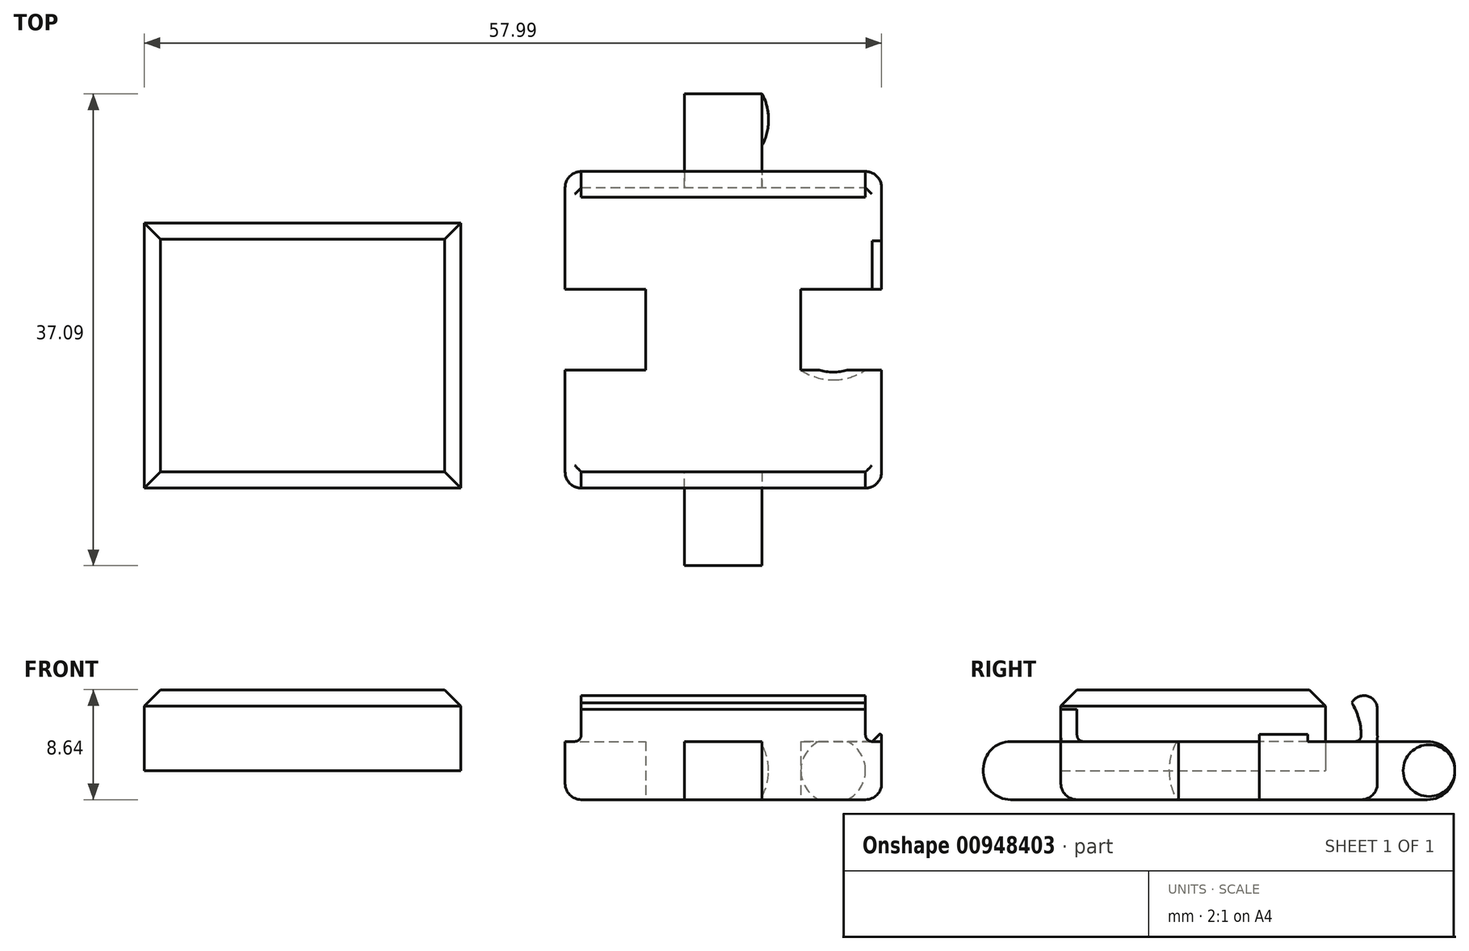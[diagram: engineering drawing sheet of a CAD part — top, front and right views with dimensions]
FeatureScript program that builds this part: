
annotation { "Feature Type Name" : "Feature", "Feature Type Description" : "" }
export const myFeature = defineFeature(function(context is Context, id is Id, definition is map)
    precondition{}
    {
        {
            var Q0;
            Q0=qCreatedBy(makeId("Top.planeOp"),FACE);
            var sketch = newSketch(context, id + "F0", { "sketchPlane" : qUnion([Q0])});
            skLineSegment(sketch, "E0.bottom", {"start": v(0, 0) * mm, "end": v(9.4, 0) * mm});
            skLineSegment(sketch, "E0.top", {"start": v(0, 24.9) * mm, "end": v(9.4, 24.9) * mm});
            skLineSegment(sketch, "E0.left", {"start": v(0, 0) * mm, "end": v(0, 9.27) * mm});
            skLineSegment(sketch, "E1", {"start": v(0, 12.45) * mm, "end": v(24.9, 12.45) * mm, "construction": true});
            skLineSegment(sketch, "E2", {"start": v(12.45, 24.9) * mm, "end": v(12.45, 0) * mm, "construction": true});
            skLineSegment(sketch, "E3", {"start": v(9.4, 24.9) * mm, "end": v(9.4, 30.99) * mm});
            skLineSegment(sketch, "E4", {"start": v(9.4, 30.99) * mm, "end": v(15.5, 30.99) * mm});
            skLineSegment(sketch, "E5", {"start": v(15.5, 30.99) * mm, "end": v(15.5, 24.9) * mm});
            skLineSegment(sketch, "E6", {"start": v(9.4, 0) * mm, "end": v(9.4, -6.1) * mm});
            skLineSegment(sketch, "E7", {"start": v(9.4, -6.1) * mm, "end": v(15.5, -6.1) * mm});
            skLineSegment(sketch, "E8", {"start": v(15.5, -6.1) * mm, "end": v(15.5, 0) * mm});
            skLineSegment(sketch, "E9.trimOffspring", {"start": v(15.5, 24.9) * mm, "end": v(24.9, 24.9) * mm});
            skLineSegment(sketch, "E10.trimOffspring", {"start": v(15.5, 0) * mm, "end": v(24.9, 0) * mm});
            skLineSegment(sketch, "E11", {"start": v(24.9, 15.62) * mm, "end": v(18.54, 15.62) * mm});
            skLineSegment(sketch, "E12", {"start": v(18.54, 15.62) * mm, "end": v(18.54, 9.27) * mm});
            skLineSegment(sketch, "E13", {"start": v(18.54, 9.27) * mm, "end": v(24.9, 9.27) * mm});
            skLineSegment(sketch, "E14", {"start": v(0, 15.62) * mm, "end": v(6.35, 15.62) * mm});
            skLineSegment(sketch, "E15", {"start": v(6.35, 15.62) * mm, "end": v(6.35, 9.27) * mm});
            skLineSegment(sketch, "E16", {"start": v(6.35, 9.27) * mm, "end": v(0, 9.27) * mm});
            skLineSegment(sketch, "E17.trimOffspring", {"start": v(0, 15.62) * mm, "end": v(0, 24.9) * mm});
            skLineSegment(sketch, "E18.trimOffspring", {"start": v(24.9, 15.62) * mm, "end": v(24.9, 24.9) * mm});
            skLineSegment(sketch, "E19", {"start": v(24.9, 0) * mm, "end": v(24.9, 9.27) * mm});
            skLineSegment(sketch, "E20", {"start": v(24.9, 9.27) * mm, "end": v(24.9, 15.62) * mm, "construction": true});
            skLineSegment(sketch, "E21", {"start": v(0, 9.27) * mm, "end": v(0, 15.62) * mm, "construction": true});
            skSolve(sketch);
        }
        {
            var Q0;
            Q0=makeQuery(id+"F0.imprint","IMPRINT",FACE,{"disambiguationData":[TD([[makeQuery(id+"F0.imprint","IMPRINT",EDGE,{"derivedFrom":sQuery(id+"F0.wireOp",EDGE,"E0.bottom")}),1.0]])]});
            extrude(context, id + "F1", {"entities" : qUnion([Q0]), "depth" : 4.57 * mm, "offsetDistance" : 25.4 * mm});
        }
        {
            var Q0;
            Q0=makeQuery(id+"F1.opExtrude","CAP_EDGE",EDGE,{"disambiguationData":[OSD([sQuery(id+"F0.wireOp",EDGE,"E4")])],"isStart":false});
            var Q1;
            Q1=makeQuery(id+"F1.opExtrude","CAP_EDGE",EDGE,{"disambiguationData":[OSD([sQuery(id+"F0.wireOp",EDGE,"E7")])],"isStart":false});
            var Q2;
            Q2=makeQuery(id+"F1.opExtrude","CAP_EDGE",EDGE,{"disambiguationData":[OSD([sQuery(id+"F0.wireOp",EDGE,"E7")])],"isStart":true});
            var Q3;
            Q3=makeQuery(id+"F1.opExtrude","CAP_EDGE",EDGE,{"disambiguationData":[OSD([sQuery(id+"F0.wireOp",EDGE,"E4")])],"isStart":true});
            fillet(context, id + "F2", {"entities" : qUnion([Q0, Q1, Q2, Q3]), "radius" : 2.16 * mm, "tangentPropagation" : true, "allowEdgeOverflow" : false});
        }
        {
            var Q0;
            Q0=makeQuery(id+"F1.opExtrude","CAP_EDGE",EDGE,{"disambiguationData":[OSD([sQuery(id+"F0.wireOp",EDGE,"E0.top")])],"isStart":true});
            var Q1;
            Q1=makeQuery(id+"F1.opExtrude","CAP_EDGE",EDGE,{"disambiguationData":[OSD([sQuery(id+"F0.wireOp",EDGE,"E9.trimOffspring")])],"isStart":true});
            var Q2;
            Q2=makeQuery(id+"F1.opExtrude","CAP_EDGE",EDGE,{"disambiguationData":[OSD([sQuery(id+"F0.wireOp",EDGE,"E10.trimOffspring")])],"isStart":true});
            var Q3;
            Q3=makeQuery(id+"F1.opExtrude","CAP_EDGE",EDGE,{"disambiguationData":[OSD([sQuery(id+"F0.wireOp",EDGE,"E0.bottom")])],"isStart":true});
            fillet(context, id + "F3", {"entities" : qUnion([Q0, Q1, Q2, Q3]), "radius" : 1.27 * mm, "tangentPropagation" : true, "allowEdgeOverflow" : false});
        }
        {
            var Q0;
            Q0=makeQuery(id+"F1.opExtrude","CAP_FACE",FACE,{"disambiguationData":[OSD([sQuery(id+"F0.wireOp",EDGE,"E0.bottom"),sQuery(id+"F0.wireOp",EDGE,"E0.top"),sQuery(id+"F0.wireOp",EDGE,"E0.left"),sQuery(id+"F0.wireOp",EDGE,"E3"),sQuery(id+"F0.wireOp",EDGE,"E4"),sQuery(id+"F0.wireOp",EDGE,"E5"),sQuery(id+"F0.wireOp",EDGE,"E6"),sQuery(id+"F0.wireOp",EDGE,"E7"),sQuery(id+"F0.wireOp",EDGE,"E8"),sQuery(id+"F0.wireOp",EDGE,"E9.trimOffspring"),sQuery(id+"F0.wireOp",EDGE,"E10.trimOffspring"),sQuery(id+"F0.wireOp",EDGE,"E11"),sQuery(id+"F0.wireOp",EDGE,"E12"),sQuery(id+"F0.wireOp",EDGE,"E13"),sQuery(id+"F0.wireOp",EDGE,"E14"),sQuery(id+"F0.wireOp",EDGE,"E15"),sQuery(id+"F0.wireOp",EDGE,"E16"),sQuery(id+"F0.wireOp",EDGE,"E17.trimOffspring"),sQuery(id+"F0.wireOp",EDGE,"E18.trimOffspring"),sQuery(id+"F0.wireOp",EDGE,"E19")])],"isStart":true});
            cPlane(context, id + "F4", {"entities" : qUnion([Q0]), "cplaneType" : CPlaneType.OFFSET, "offset" : 2.3 * mm, "oppositeDirection" : true, "width" : 152.4 * mm, "height" : 152.4 * mm});
        }
        {
            var Q0;
            Q0=qCreatedBy(id+"F4.planeOp",FACE);
            var sketch = newSketch(context, id + "F5", { "sketchPlane" : qUnion([Q0])});
            skLineSegment(sketch, "E22", {"start": v(9.9, -28.96) * mm, "end": v(17.45, -28.96) * mm, "construction": true});
            skLineSegment(sketch, "E23.0", {"start": v(9.4, -28.83) * mm, "end": v(9.4, -28.83) * mm});
            skLineSegment(sketch, "E24", {"start": v(15.5, -30.99) * mm, "end": v(9.14, -30.99) * mm, "construction": true});
            skLineSegment(sketch, "E25.0", {"start": v(15.5, -28.83) * mm, "end": v(15.5, -30.99) * mm, "construction": true});
            skLineSegment(sketch, "E26", {"start": v(15.5, -28.96) * mm, "end": v(16, -28.96) * mm});
            skArc(sketch, "E27", {"start": v(15.5, -30.99) * mm, "mid": v(15.87, -30) * mm, "end": v(16, -28.96) * mm});
            skLineSegment(sketch, "E28", {"start": v(15.5, -30.99) * mm, "end": v(15.5, -28.96) * mm});
            skSolve(sketch);
        }
        {
            var Q0;
            Q0=makeQuery(id+"F5.imprint","IMPRINT",FACE,{"disambiguationData":[TD([[makeQuery(id+"F5.imprint","IMPRINT",EDGE,{"derivedFrom":sQuery(id+"F5.wireOp",EDGE,"E26")}),-1.0]])]});
            var Q1;
            Q1=sQuery(id+"F5.wireOp",EDGE,"E27");
            var Q2;
            Q2=sQuery(id+"F5.wireOp",EDGE,"E22");
            revolve(context, id + "F6", {"operationType" : NewBodyOperationType.ADD, "surfaceOperationType" : NewSurfaceOperationType.NEW, "entities" : qUnion([Q0]), "surfaceEntities" : qUnion([Q1]), "axis" : qUnion([Q2]), "revolveType" : RevolveType.FULL});
        }
        {
            var Q0;
            Q0=makeQuery(id+"F1.opExtrude","SWEPT_FACE",FACE,{"disambiguationData":[OSD([sQuery(id+"F0.wireOp",EDGE,"E9.trimOffspring")])]});
            cPlane(context, id + "F7", {"entities" : qUnion([Q0]), "cplaneType" : CPlaneType.OFFSET, "offset" : 12.45 * mm, "oppositeDirection" : true, "width" : 152.4 * mm, "height" : 152.4 * mm});
        }
        {
            var Q0;
            Q0=makeQuery(id+"F1.opExtrude","CAP_EDGE",EDGE,{"disambiguationData":[OSD([sQuery(id+"F0.wireOp",EDGE,"E19")])],"isStart":true});
            var Q1;
            Q1=makeQuery(id+"F1.opExtrude","CAP_EDGE",EDGE,{"disambiguationData":[OSD([sQuery(id+"F0.wireOp",EDGE,"E18.trimOffspring")])],"isStart":true});
            var Q2;
            Q2=makeQuery(id+"F1.opExtrude","CAP_EDGE",EDGE,{"disambiguationData":[OSD([sQuery(id+"F0.wireOp",EDGE,"E17.trimOffspring")])],"isStart":true});
            var Q3;
            Q3=makeQuery(id+"F1.opExtrude","CAP_EDGE",EDGE,{"disambiguationData":[OSD([sQuery(id+"F0.wireOp",EDGE,"E0.left")])],"isStart":true});
            fillet(context, id + "F8", {"entities" : qUnion([Q0, Q1, Q2, Q3]), "radius" : 1.27 * mm, "tangentPropagation" : true, "allowEdgeOverflow" : false});
        }
        {
            var Q0;
            Q0=qCreatedBy(id+"F4.planeOp",FACE);
            var sketch = newSketch(context, id + "F9", { "sketchPlane" : qUnion([Q0])});
            skPoint(sketch, "E29.0", {"position": v(18.54, -12.45) * mm});
            skLineSegment(sketch, "E30.0", {"start": v(18.54, -15.62) * mm, "end": v(18.54, -9.27) * mm, "construction": true});
            skLineSegment(sketch, "E31.0", {"start": v(18.54, -9.27) * mm, "end": v(23.62, -9.27) * mm, "construction": true});
            skLineSegment(sketch, "E32.0", {"start": v(23.62, -15.62) * mm, "end": v(18.54, -15.62) * mm, "construction": true});
            skLineSegment(sketch, "E33", {"start": v(18.54, -9.27) * mm, "end": v(21.08, -9.27) * mm});
            skLineSegment(sketch, "E34", {"start": v(21.08, -9.27) * mm, "end": v(21.08, -8.5) * mm});
            skArc(sketch, "E35", {"start": v(21.08, -8.5) * mm, "mid": v(19.76, -8.7) * mm, "end": v(18.54, -9.27) * mm});
            skLineSegment(sketch, "E36", {"start": v(21.08, -9.27) * mm, "end": v(21.08, -12.64) * mm, "construction": true});
            skSolve(sketch);
        }
        {
            var Q0;
            Q0=makeQuery(id+"F9.imprint","IMPRINT",FACE,{"disambiguationData":[TD([[makeQuery(id+"F9.imprint","IMPRINT",EDGE,{"derivedFrom":sQuery(id+"F9.wireOp",EDGE,"E33")}),1.0]])]});
            var Q1;
            Q1=sQuery(id+"F9.wireOp",EDGE,"E36");
            revolve(context, id + "F10", {"operationType" : NewBodyOperationType.REMOVE, "surfaceOperationType" : NewSurfaceOperationType.NEW, "entities" : qUnion([Q0]), "axis" : qUnion([Q1]), "revolveType" : RevolveType.FULL, "oppositeDirection" : true});
        }
        {
            var Q0;
            Q0=makeQuery(id+"F1.opExtrude","SWEPT_FACE",FACE,{"disambiguationData":[OSD([sQuery(id+"F0.wireOp",EDGE,"E18.trimOffspring")])]});
            cPlane(context, id + "F11", {"entities" : qUnion([Q0]), "cplaneType" : CPlaneType.OFFSET, "offset" : 12.45 * mm, "oppositeDirection" : true, "width" : 152.4 * mm, "height" : 152.4 * mm});
        }
        {
            var Q0;
            Q0=makeQuery(id+"F1.opExtrude","CAP_FACE",FACE,{"disambiguationData":[OSD([sQuery(id+"F0.wireOp",EDGE,"E0.bottom"),sQuery(id+"F0.wireOp",EDGE,"E0.top"),sQuery(id+"F0.wireOp",EDGE,"E0.left"),sQuery(id+"F0.wireOp",EDGE,"E3"),sQuery(id+"F0.wireOp",EDGE,"E4"),sQuery(id+"F0.wireOp",EDGE,"E5"),sQuery(id+"F0.wireOp",EDGE,"E6"),sQuery(id+"F0.wireOp",EDGE,"E7"),sQuery(id+"F0.wireOp",EDGE,"E8"),sQuery(id+"F0.wireOp",EDGE,"E9.trimOffspring"),sQuery(id+"F0.wireOp",EDGE,"E10.trimOffspring"),sQuery(id+"F0.wireOp",EDGE,"E11"),sQuery(id+"F0.wireOp",EDGE,"E12"),sQuery(id+"F0.wireOp",EDGE,"E13"),sQuery(id+"F0.wireOp",EDGE,"E14"),sQuery(id+"F0.wireOp",EDGE,"E15"),sQuery(id+"F0.wireOp",EDGE,"E16"),sQuery(id+"F0.wireOp",EDGE,"E17.trimOffspring"),sQuery(id+"F0.wireOp",EDGE,"E18.trimOffspring"),sQuery(id+"F0.wireOp",EDGE,"E19")])],"isStart":false});
            var sketch = newSketch(context, id + "F12", { "sketchPlane" : qUnion([Q0])});
            skLineSegment(sketch, "E37.bottom", {"start": v(1.27, 0) * mm, "end": v(23.62, 0) * mm});
            skLineSegment(sketch, "E37.top", {"start": v(1.27, 1.27) * mm, "end": v(23.62, 1.27) * mm});
            skLineSegment(sketch, "E37.left", {"start": v(1.27, 0) * mm, "end": v(1.27, 1.27) * mm});
            skLineSegment(sketch, "E37.right", {"start": v(23.62, 0) * mm, "end": v(23.62, 1.27) * mm});
            skLineSegment(sketch, "E38.bottom", {"start": v(1.27, 24.9) * mm, "end": v(23.62, 24.9) * mm});
            skLineSegment(sketch, "E38.top", {"start": v(1.27, 23.62) * mm, "end": v(23.62, 23.62) * mm});
            skLineSegment(sketch, "E38.left", {"start": v(1.27, 24.9) * mm, "end": v(1.27, 23.62) * mm});
            skLineSegment(sketch, "E38.right", {"start": v(23.62, 24.9) * mm, "end": v(23.62, 23.62) * mm});
            skLineSegment(sketch, "E39", {"start": v(12.45, 28.83) * mm, "end": v(12.45, -3.94) * mm, "construction": true});
            skLineSegment(sketch, "E40", {"start": v(18.54, 12.45) * mm, "end": v(6.35, 12.45) * mm, "construction": true});
            skLineSegment(sketch, "E41", {"start": v(1.27, 1.27) * mm, "end": v(1.27, 23.62) * mm, "construction": true});
            skLineSegment(sketch, "E42", {"start": v(23.62, 1.27) * mm, "end": v(23.62, 23.62) * mm, "construction": true});
            skSolve(sketch);
        }
        {
            var Q0;
            Q0=makeQuery(id+"F12.imprint","IMPRINT",FACE,{"disambiguationData":[TD([[makeQuery(id+"F12.imprint","IMPRINT",EDGE,{"derivedFrom":sQuery(id+"F12.wireOp",EDGE,"E37.top")}),-1.0]])]});
            var Q1;
            Q1=makeQuery(id+"F12.imprint","IMPRINT",FACE,{"disambiguationData":[TD([[makeQuery(id+"F12.imprint","IMPRINT",EDGE,{"derivedFrom":sQuery(id+"F12.wireOp",EDGE,"E38.top")}),1.0]])]});
            extrude(context, id + "F13", {"entities" : qUnion([Q0, Q1]), "operationType" : NewBodyOperationType.ADD, "depth" : 2.54 * mm, "offsetDistance" : 25.4 * mm});
        }
        {
            var Q0;
            Q0=makeQuery(id+"F13.opExtrude","SWEPT_FACE",FACE,{"disambiguationData":[OSD([sQuery(id+"F12.wireOp",EDGE,"E37.right")])]});
            var sketch = newSketch(context, id + "F14", { "sketchPlane" : qUnion([Q0])});
            skLineSegment(sketch, "E43", {"start": v(0, 7.11) * mm, "end": v(1.07, 7.11) * mm, "construction": true});
            skArc(sketch, "E44", {"start": v(0, 7.11) * mm, "mid": v(0.8, 8.15) * mm, "end": v(2, 7.61) * mm});
            skLineSegment(sketch, "E45", {"start": v(1.07, 7.11) * mm, "end": v(2, 7.61) * mm, "construction": true});
            skLineSegment(sketch, "E46", {"start": v(1.27, 7.11) * mm, "end": v(2, 7.61) * mm});
            skLineSegment(sketch, "E47.1", {"start": v(24.9, 7.11) * mm, "end": v(24.9, 4.57) * mm, "construction": true});
            skArc(sketch, "E48", {"start": v(24.9, 7.11) * mm, "mid": v(24.08, 8.15) * mm, "end": v(22.88, 7.61) * mm, "construction": true});
            skLineSegment(sketch, "E49", {"start": v(23.83, 7.11) * mm, "end": v(22.88, 7.61) * mm, "construction": true});
            skArc(sketch, "E50", {"start": v(24.9, 7.11) * mm, "mid": v(24.08, 8.15) * mm, "end": v(22.88, 7.61) * mm});
            skLineSegment(sketch, "E51", {"start": v(23.62, 7.11) * mm, "end": v(22.88, 7.61) * mm});
            skLineSegment(sketch, "E52", {"start": v(23.62, 7.11) * mm, "end": v(24.9, 7.11) * mm});
            skSolve(sketch);
        }
        {
            var Q0;
            Q0=makeQuery(id+"F14.imprint","IMPRINT",FACE,{"disambiguationData":[TD([[makeQuery(id+"F14.imprint","IMPRINT",EDGE,{"derivedFrom":sQuery(id+"F14.wireOp",EDGE,"E44")}),-1.0]])]});
            var Q1;
            Q1=makeQuery(id+"F14.imprint","IMPRINT",FACE,{"disambiguationData":[TD([[makeQuery(id+"F14.imprint","IMPRINT",EDGE,{"derivedFrom":sQuery(id+"F14.wireOp",EDGE,"E50")}),1.0]])]});
            extrude(context, id + "F15", {"entities" : qUnion([Q0, Q1]), "operationType" : NewBodyOperationType.ADD, "oppositeDirection" : true, "depth" : 22.35 * mm, "offsetDistance" : 25.4 * mm});
        }
        {
            var Q0;
            Q0=makeQuery(id+"F15.boolean.opBoolean","MERGE",EDGE,{"derivedFrom":[makeQuery(id+"F13.opExtrude","CAP_EDGE",EDGE,{"disambiguationData":[OSD([sQuery(id+"F12.wireOp",EDGE,"E38.top")])],"isStart":false}),makeQuery(id+"F15.opExtrude","SWEPT_EDGE",EDGE,{"disambiguationData":[OSD([sQuery(id+"F14.wireOp",EDGE,"E51"),sQuery(id+"F14.wireOp",EDGE,"E52")])]})]});
            var Q1;
            {var subQ0=sQuery(id+"F12.wireOp",EDGE,"E37.top");Q1=makeQuery(id+"F15.boolean.opBoolean","MERGE",EDGE,{"derivedFrom":[makeQuery(id+"F13.opExtrude","CAP_EDGE",EDGE,{"disambiguationData":[OSD([subQ0])],"isStart":false}),makeQuery(id+"F15.opExtrude","SWEPT_EDGE",EDGE,{"disambiguationData":[OSD([subQ0,sQuery(id+"F12.wireOp",EDGE,"E37.right"),sQuery(id+"F14.wireOp",EDGE,"E46")])]})]});}
            fillet(context, id + "F16", {"entities" : qUnion([Q0, Q1]), "radius" : 5.08 * mm, "tangentPropagation" : true, "allowEdgeOverflow" : false});
        }
        {
            var Q0;
            Q0=makeQuery(id+"F13.opExtrude","CAP_EDGE",EDGE,{"disambiguationData":[OSD([sQuery(id+"F12.wireOp",EDGE,"E38.top")])],"isStart":true});
            var Q1;
            Q1=makeQuery(id+"F13.opExtrude","CAP_EDGE",EDGE,{"disambiguationData":[OSD([sQuery(id+"F12.wireOp",EDGE,"E37.top")])],"isStart":true});
            var Q2;
            Q2=makeQuery(id+"F13.opExtrude","CAP_EDGE",EDGE,{"disambiguationData":[OSD([sQuery(id+"F12.wireOp",EDGE,"E37.right")])],"isStart":true});
            var Q3;
            Q3=makeQuery(id+"F13.opExtrude","CAP_EDGE",EDGE,{"disambiguationData":[OSD([sQuery(id+"F12.wireOp",EDGE,"E38.right")])],"isStart":true});
            var Q4;
            Q4=makeQuery(id+"F13.opExtrude","CAP_EDGE",EDGE,{"disambiguationData":[OSD([sQuery(id+"F12.wireOp",EDGE,"E38.left")])],"isStart":true});
            var Q5;
            Q5=makeQuery(id+"F13.opExtrude","CAP_EDGE",EDGE,{"disambiguationData":[OSD([sQuery(id+"F12.wireOp",EDGE,"E37.left")])],"isStart":true});
            fillet(context, id + "F17", {"entities" : qUnion([Q0, Q1, Q2, Q3, Q4, Q5]), "radius" : 0.5 * mm, "tangentPropagation" : true, "allowEdgeOverflow" : false});
        }
        {
            var Q0;
            Q0=qCreatedBy(id+"F4.planeOp",FACE);
            var sketch = newSketch(context, id + "F18", { "sketchPlane" : qUnion([Q0])});
            skLineSegment(sketch, "E53.bottom", {"start": v(-8.2, 0) * mm, "end": v(-33.1, 0) * mm});
            skLineSegment(sketch, "E53.top", {"start": v(-8.2, -20.83) * mm, "end": v(-33.1, -20.83) * mm});
            skLineSegment(sketch, "E53.left", {"start": v(-8.2, 0) * mm, "end": v(-8.2, -20.83) * mm});
            skLineSegment(sketch, "E53.right", {"start": v(-33.1, 0) * mm, "end": v(-33.1, -20.83) * mm});
            skSolve(sketch);
        }
        {
            var Q0;
            Q0=makeQuery(id+"F18.imprint","IMPRINT",FACE,{"disambiguationData":[TD([[makeQuery(id+"F18.imprint","IMPRINT",EDGE,{"derivedFrom":sQuery(id+"F18.wireOp",EDGE,"E53.bottom")}),1.0]])]});
            extrude(context, id + "F19", {"entities" : qUnion([Q0]), "oppositeDirection" : true, "depth" : 6.35 * mm, "offsetDistance" : 25.4 * mm});
        }
        {
            var Q0;
            Q0=makeQuery(id+"F19.opExtrude","CAP_FACE",FACE,{"disambiguationData":[OSD([sQuery(id+"F18.wireOp",EDGE,"E53.bottom"),sQuery(id+"F18.wireOp",EDGE,"E53.top"),sQuery(id+"F18.wireOp",EDGE,"E53.left"),sQuery(id+"F18.wireOp",EDGE,"E53.right")])],"isStart":false});
            chamfer(context, id + "F20", {"entities" : qUnion([Q0]), "width" : 1.27 * mm, "tangentPropagation" : true});
        }
        {
            var Q0;
            {var subQ0=sQuery(id+"F0.wireOp",EDGE,"E18.trimOffspring");var subQ1=sQuery(id+"F0.wireOp",EDGE,"E19");var subQ2=sQuery(id+"F0.wireOp",EDGE,"E17.trimOffspring");var subQ3=sQuery(id+"F0.wireOp",EDGE,"E16");var subQ4=sQuery(id+"F0.wireOp",EDGE,"E15");var subQ5=sQuery(id+"F0.wireOp",EDGE,"E14");var subQ6=sQuery(id+"F0.wireOp",EDGE,"E13");var subQ7=sQuery(id+"F0.wireOp",EDGE,"E12");var subQ8=sQuery(id+"F0.wireOp",EDGE,"E11");var subQ9=sQuery(id+"F0.wireOp",EDGE,"E10.trimOffspring");var subQ10=sQuery(id+"F0.wireOp",EDGE,"E9.trimOffspring");var subQ11=sQuery(id+"F0.wireOp",EDGE,"E8");var subQ12=sQuery(id+"F0.wireOp",EDGE,"E7");var subQ13=sQuery(id+"F0.wireOp",EDGE,"E6");var subQ14=sQuery(id+"F0.wireOp",EDGE,"E5");var subQ15=sQuery(id+"F0.wireOp",EDGE,"E4");var subQ16=sQuery(id+"F0.wireOp",EDGE,"E3");var subQ17=sQuery(id+"F0.wireOp",EDGE,"E0.left");var subQ18=sQuery(id+"F0.wireOp",EDGE,"E0.top");var subQ19=sQuery(id+"F0.wireOp",EDGE,"E0.bottom");Q0=makeQuery(id+"FC4Avln7rrRuZGU_1.1.F10.boolean.opBoolean","SPLIT",FACE,{"disambiguationData":[TD([makeQuery(id+"F1.opExtrude","CAP_FACE",FACE,{"disambiguationData":[OSD([subQ19,subQ18,subQ17,subQ16,subQ15,subQ14,subQ13,subQ12,subQ11,subQ10,subQ9,subQ8,subQ7,subQ6,subQ5,subQ4,subQ3,subQ2,subQ0,subQ1])],"isStart":true}),makeQuery(id+"F1.opExtrude","CAP_FACE",FACE,{"disambiguationData":[OSD([subQ19,subQ18,subQ17,subQ16,subQ15,subQ14,subQ13,subQ12,subQ11,subQ10,subQ9,subQ8,subQ7,subQ6,subQ5,subQ4,subQ3,subQ2,subQ0,subQ1])],"isStart":false}),makeQuery(id+"F1.opExtrude","SWEPT_FACE",FACE,{"disambiguationData":[OSD([subQ0])]}),makeQuery(id+"F8.opFillet","BLEND_FACE",FACE,{"disambiguationData":[OSD([subQ0])]}),makeQuery(id+"FC4Avln7rrRuZGU_1.1.F10.opRevolve","SWEPT_FACE",FACE,{"disambiguationData":[OSD([sQuery(id+"F9.wireOp",EDGE,"E35")])]})])],"derivedFrom":makeQuery(id+"F1.opExtrude","SWEPT_FACE",FACE,{"disambiguationData":[OSD([subQ8])]})});}
            var sketch = newSketch(context, id + "F21", { "sketchPlane" : qUnion([Q0])});
            skLineSegment(sketch, "E54", {"start": v(24.9, 4.57) * mm, "end": v(24.9, 5.33) * mm});
            skLineSegment(sketch, "E55", {"start": v(24.9, 5.33) * mm, "end": v(24.14, 4.57) * mm});
            skLineSegment(sketch, "E56", {"start": v(24.14, 4.57) * mm, "end": v(24.9, 4.57) * mm});
            skSolve(sketch);
        }
        {
            var Q0;
            Q0=makeQuery(id+"F21.imprint","IMPRINT",FACE,{"disambiguationData":[TD([[makeQuery(id+"F21.imprint","IMPRINT",EDGE,{"derivedFrom":sQuery(id+"F21.wireOp",EDGE,"E54")}),1.0]])]});
            extrude(context, id + "F22", {"entities" : qUnion([Q0]), "operationType" : NewBodyOperationType.ADD, "oppositeDirection" : true, "depth" : 3.8 * mm, "offsetDistance" : 25.4 * mm});
        }
        {
            var Q0;
            Q0=makeQuery(id+"F22.opExtrude","SWEPT_EDGE",EDGE,{"disambiguationData":[OSD([sQuery(id+"F21.wireOp",EDGE,"E54"),sQuery(id+"F21.wireOp",EDGE,"E55")])]});
            var Q1;
            Q1=makeQuery(id+"FZW6YWHvyj64x5S_2.1.F22.opExtrude","SWEPT_EDGE",EDGE,{"disambiguationData":[OSD([sQuery(id+"F21.wireOp",EDGE,"E54"),sQuery(id+"F21.wireOp",EDGE,"E55")])]});
            var Q2;
            Q2=makeQuery(id+"FJ7cX2PqjQGeN0S_2.1.FZW6YWHvyj64x5S_2.1.F22.opExtrude","SWEPT_EDGE",EDGE,{"disambiguationData":[OSD([sQuery(id+"F21.wireOp",EDGE,"E54"),sQuery(id+"F21.wireOp",EDGE,"E55")])]});
            var Q3;
            Q3=makeQuery(id+"FJ7cX2PqjQGeN0S_2.1.F22.opExtrude","SWEPT_EDGE",EDGE,{"disambiguationData":[OSD([sQuery(id+"F21.wireOp",EDGE,"E54"),sQuery(id+"F21.wireOp",EDGE,"E55")])]});
            fillet(context, id + "F23", {"entities" : qUnion([Q0, Q1, Q2, Q3]), "radius" : 0.13 * mm, "tangentPropagation" : true, "allowEdgeOverflow" : false});
        }
    });
